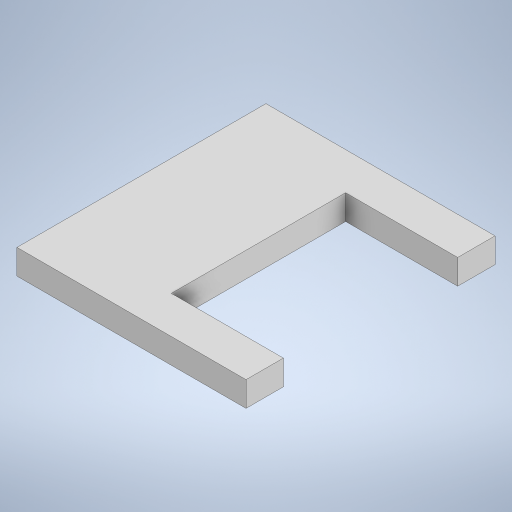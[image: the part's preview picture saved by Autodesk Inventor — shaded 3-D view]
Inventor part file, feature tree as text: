
AUTODESK INVENTOR PART (.ipt)
format: ipt  version: 2024 (Build 280153000, 153)  size: 228,352 bytes
history: native  units: mm
features: sketch x3, extrude x2
ambient origin geometry x8: Origin, YZ Plane, XZ Plane, XY Plane, X Axis, Y Axis, Z Axis, Center Point
bodies: Solid1 (feature_tree)
feature tree (5):
  sketch  "Sketch1"  dims[d0=100.0mm d1=92.0mm]
  extrude  "Extrusion1"  Depth=92.0mm
  extrude  "Extrusion2"  Depth=70.0mm
  sketch  "Sketch2"  dims[d2=10.0mm d3=0.0mm d4=70.0mm]
  sketch  "Sketch3"  dims[d5=15.0mm d6=15.0mm d7=45.0mm d8=100.0mm d9=0.0mm]
